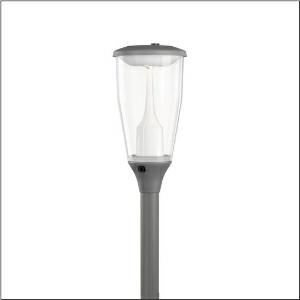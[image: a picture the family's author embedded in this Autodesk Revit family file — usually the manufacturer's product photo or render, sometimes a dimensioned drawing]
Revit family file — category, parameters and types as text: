
# Revit family: dl_11_iq___st1_2a_5xa5565ew14h000022_25f9
name_source: partatom
category: Lighting Fixtures
units: mm (PartAtom-declared; Revit-internal decimal feet)

## family parameters
Cut with Voids When Loaded = No
Host = Face
Light Source = No
Part Type = Normal
Room Calculation Point = No
Round Connector Dimension = Use Diameter
Shared = No

## types (1)
- --- (1 x LED, 1560 lm, 10.7 W, 3000K)
    Apparent Load = 11 VA
    CIE Flux Codes = 24 63 94 96 100
    Color Rendering = 70
    Color Temperature = 3000K
    Default Elevation = 1800 mm
    Description = DL 11 iQ, mast luminaire, Module 540 iQ-SR, primary light control with 3 zone facetted reflector, of plastic, silver coated, highly specular, structured, primary optical cover: cover, of PMMA, transparent, light distribution: ST1.2a, light emission: direct distribution, primary light characteristic: asymmetric, installation type: post-top, LED, High Power LED, rated luminous flux: 1.560lm, luminous efficacy: 146lm/W, light colour: 730, colour temperature: 3000K, control gear: iQ-Street Remote, D4i with power reduction, control: pre-setting: logarithmic dimming characteristic, Street-Remote, Auto-Match, Temp-Guard, Lumen-Switch, Night-Set, Smart-Wire, Light-Fading, Desk-Remote (wireless, voltage-free reading and setting of iQ features in the workshop via application-optimized NFC function/RFID function), optimised constant luminous flux control (CLO 2.0), mains connection: 220..240V, AC, 50/60Hz, connection cable pre-assembled, cable length: 5,5m, start of lifetime: 11W, end of service life: 11W, reduction: 6W, luminaire housing, upper part, of diecast aluminium, coated, SITECO metallic grey (DB 702S), spigot size: 60mm (post-top), mounting height: 3..5m, post-top mast mounting element, of diecast aluminium, coated, SITECO metallic grey (DB 702S), Module 540 iQ-SR, traffic white (RAL 9016), equipment: standard, Smart Interface above and design motion detector below, protection rating (complete): IP65, insulation class (complete): insulation class II (safety insulation), certification: CE, ENEC, ENEC+, VDE, impact resistance: IK07, packaging unit: 1 piece

Light Distribution: ST1.2a
    Height = 665 mm
    Lamp = 1 x LED
    Lamp Light Flux = 1560 lm
    Lamp Power = 10.7 W
    Lamp count = 1
    Length = 334 mm
    Luminous efficacy = 146 lm/W
    Manufacturer = Siteco
    ModVariant = No
    Model = 5XA5565EW14H000022
    Number of Poles = 1
    OnlyDefault = Yes
    Power Factor = 1
    Product Name = DL 11 iQ | ST1.2a
    Product group = mast luminaire | pylon top
    ProductGroupID = 6100
    Protection Class = Protection class II
    Protection Degree = IP 65
    RLX_Detail_Level = 1
    RLX_Emergency_Light_Flux = 0 lm
    RLX_Emergency_Type = 0
    RLX_Emergency_Type_DB = No
    RlxData = <blob elided: 158661 chars, md5=4f2a73d4>
    Socket = socket
    Standby Power = 0 W
    System Light Flux = 1560 lm
    System Power = 11 W
    Type Comments = factory setting: luminous flux: 100 % | dim-lin: 254 | 419 mA
    Type Image = l_1337543.jpg
    URL = http://relux.com
    VarID = @adj_098889
    Voltage = 0 V
    Weight = 0.00 kg
    Width = 0 mm  [stored 0 ft]

note: [stored X ft] marks values corroborated as IEEE doubles in the binary element streams (Revit-internal decimal feet)

## geometry (parser evidence)
native form markers: Blend x4, Sweep x10
no freeform markers — native parametric forms only
